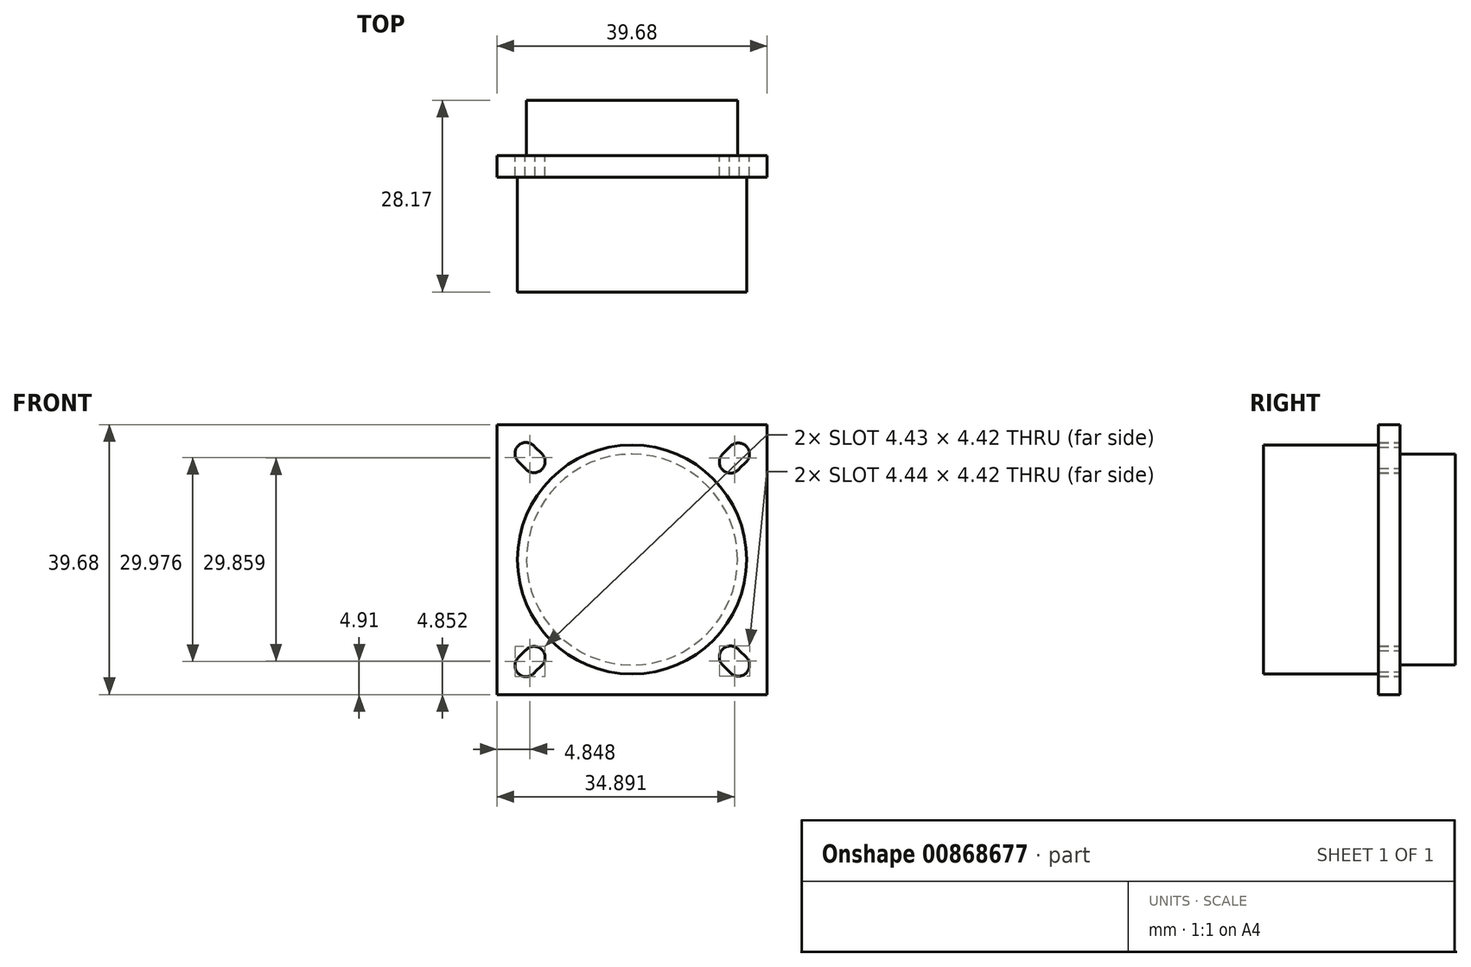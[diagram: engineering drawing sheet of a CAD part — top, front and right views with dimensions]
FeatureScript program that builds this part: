
annotation { "Feature Type Name" : "Feature", "Feature Type Description" : "" }
export const myFeature = defineFeature(function(context is Context, id is Id, definition is map)
    precondition{}
    {
        {
            var Q0;
            Q0=qCreatedBy(makeId("Front.planeOp"),FACE);
            var sketch = newSketch(context, id + "F0", { "sketchPlane" : qUnion([Q0])});
            skLineSegment(sketch, "E0.bottom", {"start": v(-19.84, 19.84) * mm, "end": v(19.84, 19.84) * mm});
            skLineSegment(sketch, "E0.top", {"start": v(-19.84, -19.84) * mm, "end": v(19.84, -19.84) * mm});
            skLineSegment(sketch, "E0.left", {"start": v(-19.84, 19.84) * mm, "end": v(-19.84, -19.84) * mm});
            skLineSegment(sketch, "E0.right", {"start": v(19.84, 19.84) * mm, "end": v(19.84, -19.84) * mm});
            skPoint(sketch, "E0.middle", {"position": v(0, 0) * mm});
            skCircle(sketch, "E1", {"center": v(0, 0) * mm, "radius": 16.83 * mm});
            skCircle(sketch, "E2", {"center": v(0, 0) * mm, "radius": 17.46 * mm});
            skLineSegment(sketch, "E3", {"start": v(-19.84, 19.84) * mm, "end": v(19.84, -19.84) * mm, "construction": true});
            skLineSegment(sketch, "E4", {"start": v(-19.84, -19.84) * mm, "end": v(19.84, 19.84) * mm, "construction": true});
            skArc(sketch, "E5", {"start": v(-14.25, 16.52) * mm, "mid": v(-16.64, 16.82) * mm, "end": v(-16.72, 14.42) * mm});
            skArc(sketch, "E6", {"start": v(-15.7, 13.42) * mm, "mid": v(-13.32, 13.18) * mm, "end": v(-13.27, 15.56) * mm});
            skLineSegment(sketch, "E7", {"start": v(-15.7, 13.42) * mm, "end": v(-16.72, 14.42) * mm});
            skLineSegment(sketch, "E8", {"start": v(-14.25, 16.52) * mm, "end": v(-13.27, 15.56) * mm});
            skArc(sketch, "E9", {"start": v(15.79, -13.4) * mm, "mid": v(13.4, -13.1) * mm, "end": v(13.32, -15.5) * mm});
            skArc(sketch, "E10", {"start": v(14.34, -16.49) * mm, "mid": v(16.72, -16.74) * mm, "end": v(16.77, -14.35) * mm});
            skLineSegment(sketch, "E11", {"start": v(14.34, -16.49) * mm, "end": v(13.32, -15.5) * mm});
            skLineSegment(sketch, "E12", {"start": v(15.79, -13.4) * mm, "end": v(16.77, -14.35) * mm});
            skLineSegment(sketch, "E13", {"start": v(-19.84, 0) * mm, "end": v(19.84, 0) * mm, "construction": true});
            skLineSegment(sketch, "E14.MirrorCS", {"start": v(-14.25, -16.52) * mm, "end": v(-13.27, -15.56) * mm});
            skLineSegment(sketch, "E15.MirrorCS", {"start": v(-15.7, -13.42) * mm, "end": v(-16.72, -14.42) * mm});
            skArc(sketch, "E16.MirrorCS", {"start": v(-14.25, -16.52) * mm, "mid": v(-16.64, -16.82) * mm, "end": v(-16.72, -14.42) * mm});
            skArc(sketch, "E17.MirrorCS", {"start": v(-15.7, -13.42) * mm, "mid": v(-13.32, -13.18) * mm, "end": v(-13.27, -15.56) * mm});
            skLineSegment(sketch, "E18.MirrorCS", {"start": v(15.79, 13.4) * mm, "end": v(16.77, 14.35) * mm});
            skLineSegment(sketch, "E19.MirrorCS", {"start": v(14.34, 16.49) * mm, "end": v(13.32, 15.5) * mm});
            skArc(sketch, "E20.MirrorCS", {"start": v(15.79, 13.4) * mm, "mid": v(13.4, 13.1) * mm, "end": v(13.32, 15.5) * mm});
            skArc(sketch, "E21.MirrorCS", {"start": v(14.34, 16.49) * mm, "mid": v(16.72, 16.74) * mm, "end": v(16.77, 14.35) * mm});
            skSolve(sketch);
        }
        {
            var Q0;
            Q0=makeQuery(id+"F0.imprint","IMPRINT",FACE,{"disambiguationData":[TD([[makeQuery(id+"F0.imprint","IMPRINT",EDGE,{"derivedFrom":sQuery(id+"F0.wireOp",EDGE,"E0.bottom")}),-1.0]])]});
            var Q1;
            Q1=makeQuery(id+"F0.imprint","IMPRINT",FACE,{"disambiguationData":[TD([[makeQuery(id+"F0.imprint","IMPRINT",EDGE,{"derivedFrom":sQuery(id+"F0.wireOp",EDGE,"E2")}),-1.0]])]});
            var Q2;
            Q2=makeQuery(id+"F0.imprint","IMPRINT",FACE,{"disambiguationData":[TD([[makeQuery(id+"F0.imprint","IMPRINT",EDGE,{"derivedFrom":sQuery(id+"F0.wireOp",EDGE,"E1")}),-1.0]])]});
            extrude(context, id + "F1", {"entities" : qUnion([Q0, Q1, Q2]), "depth" : 3.2 * mm, "offsetDistance" : 25.4 * mm});
        }
        {
            var Q0;
            Q0=makeQuery(id+"F0.imprint","IMPRINT",FACE,{"disambiguationData":[TD([[makeQuery(id+"F0.imprint","IMPRINT",EDGE,{"derivedFrom":sQuery(id+"F0.wireOp",EDGE,"E1")}),1.0]])]});
            extrude(context, id + "F2", {"entities" : qUnion([Q0]), "operationType" : NewBodyOperationType.ADD, "depth" : 20.07 * mm, "offsetDistance" : 25.4 * mm});
        }
        {
            var Q0;
            Q0=makeQuery(id+"F2.boolean.opBoolean","SPLIT",FACE,{"disambiguationData":[TD([makeQuery(id+"F2.opExtrude","SWEPT_FACE",FACE,{"disambiguationData":[OSD([sQuery(id+"F0.wireOp",EDGE,"E1")])]})])],"derivedFrom":makeQuery(id+"F1.opExtrude","CAP_FACE",FACE,{"disambiguationData":[OSD([sQuery(id+"F0.wireOp",EDGE,"E0.bottom"),sQuery(id+"F0.wireOp",EDGE,"E0.top"),sQuery(id+"F0.wireOp",EDGE,"E0.left"),sQuery(id+"F0.wireOp",EDGE,"E0.right"),sQuery(id+"F0.wireOp",EDGE,"E5"),sQuery(id+"F0.wireOp",EDGE,"E6"),sQuery(id+"F0.wireOp",EDGE,"E7"),sQuery(id+"F0.wireOp",EDGE,"E8"),sQuery(id+"F0.wireOp",EDGE,"E9"),sQuery(id+"F0.wireOp",EDGE,"E10"),sQuery(id+"F0.wireOp",EDGE,"E11"),sQuery(id+"F0.wireOp",EDGE,"E12"),sQuery(id+"F0.wireOp",EDGE,"E14.MirrorCS"),sQuery(id+"F0.wireOp",EDGE,"E15.MirrorCS"),sQuery(id+"F0.wireOp",EDGE,"E16.MirrorCS"),sQuery(id+"F0.wireOp",EDGE,"E17.MirrorCS"),sQuery(id+"F0.wireOp",EDGE,"E18.MirrorCS"),sQuery(id+"F0.wireOp",EDGE,"E19.MirrorCS"),sQuery(id+"F0.wireOp",EDGE,"E20.MirrorCS"),sQuery(id+"F0.wireOp",EDGE,"E21.MirrorCS")])],"isStart":false})});
            var sketch = newSketch(context, id + "F3", { "sketchPlane" : qUnion([Q0])});
            skCircle(sketch, "E22", {"center": v(0, 0) * mm, "radius": 15.24 * mm});
            skCircle(sketch, "E23", {"center": v(0, 0) * mm, "radius": 13.97 * mm});
            skLineSegment(sketch, "E24.bottom", {"start": v(-1.59, -15.16) * mm, "end": v(1.59, -15.16) * mm});
            skLineSegment(sketch, "E24.top", {"start": v(-1.59, -16.43) * mm, "end": v(1.59, -16.43) * mm});
            skLineSegment(sketch, "E24.left", {"start": v(-1.59, -15.16) * mm, "end": v(-1.59, -16.43) * mm});
            skLineSegment(sketch, "E24.right", {"start": v(1.59, -15.16) * mm, "end": v(1.59, -16.43) * mm});
            skSolve(sketch);
        }
        {
            var Q0;
            Q0=makeQuery(id+"F3.imprint","IMPRINT",FACE,{"disambiguationData":[TD([[makeQuery(id+"F3.imprint","IMPRINT",EDGE,{"derivedFrom":sQuery(id+"F3.wireOp",EDGE,"E23")}),-1.0]])]});
            var Q1;
            Q1=makeQuery(id+"F3.imprint","IMPRINT",FACE,{"disambiguationData":[TD([[makeQuery(id+"F3.imprint","IMPRINT",EDGE,{"derivedFrom":sQuery(id+"F3.wireOp",EDGE,"E24.top")}),1.0]])]});
            var Q2;
            {var subQ0=sQuery(id+"F3.wireOp",EDGE,"E24.bottom");Q2=makeQuery(id+"F3.imprint","IMPRINT",FACE,{"disambiguationData":[TD([[makeQuery(id+"F3.imprint","IMPRINT",EDGE,{"derivedFrom":subQ0}),-1.0]])]});}
            extrude(context, id + "F4", {"entities" : qUnion([Q0, Q1, Q2]), "operationType" : NewBodyOperationType.ADD, "depth" : 16.87 * mm, "offsetDistance" : 25.4 * mm});
        }
        {
            var Q0;
            Q0=makeQuery(id+"F1.opExtrude","CAP_FACE",FACE,{"disambiguationData":[OSD([sQuery(id+"F0.wireOp",EDGE,"E0.bottom"),sQuery(id+"F0.wireOp",EDGE,"E0.top"),sQuery(id+"F0.wireOp",EDGE,"E0.left"),sQuery(id+"F0.wireOp",EDGE,"E0.right"),sQuery(id+"F0.wireOp",EDGE,"E5"),sQuery(id+"F0.wireOp",EDGE,"E6"),sQuery(id+"F0.wireOp",EDGE,"E7"),sQuery(id+"F0.wireOp",EDGE,"E8"),sQuery(id+"F0.wireOp",EDGE,"E9"),sQuery(id+"F0.wireOp",EDGE,"E10"),sQuery(id+"F0.wireOp",EDGE,"E11"),sQuery(id+"F0.wireOp",EDGE,"E12"),sQuery(id+"F0.wireOp",EDGE,"E14.MirrorCS"),sQuery(id+"F0.wireOp",EDGE,"E15.MirrorCS"),sQuery(id+"F0.wireOp",EDGE,"E16.MirrorCS"),sQuery(id+"F0.wireOp",EDGE,"E17.MirrorCS"),sQuery(id+"F0.wireOp",EDGE,"E18.MirrorCS"),sQuery(id+"F0.wireOp",EDGE,"E19.MirrorCS"),sQuery(id+"F0.wireOp",EDGE,"E20.MirrorCS"),sQuery(id+"F0.wireOp",EDGE,"E21.MirrorCS")])],"isStart":true});
            var sketch = newSketch(context, id + "F5", { "sketchPlane" : qUnion([Q0])});
            skCircle(sketch, "E25", {"center": v(0, 0) * mm, "radius": 15.5 * mm});
            skSolve(sketch);
        }
        {
            var Q0;
            Q0=makeQuery(id+"F5.imprint","IMPRINT",FACE,{"disambiguationData":[TD([[makeQuery(id+"F5.imprint","IMPRINT",EDGE,{"derivedFrom":sQuery(id+"F5.wireOp",EDGE,"E25")}),1.0]])]});
            extrude(context, id + "F6", {"entities" : qUnion([Q0]), "operationType" : NewBodyOperationType.ADD, "depth" : 8.1 * mm, "offsetDistance" : 25.4 * mm});
        }
    });
